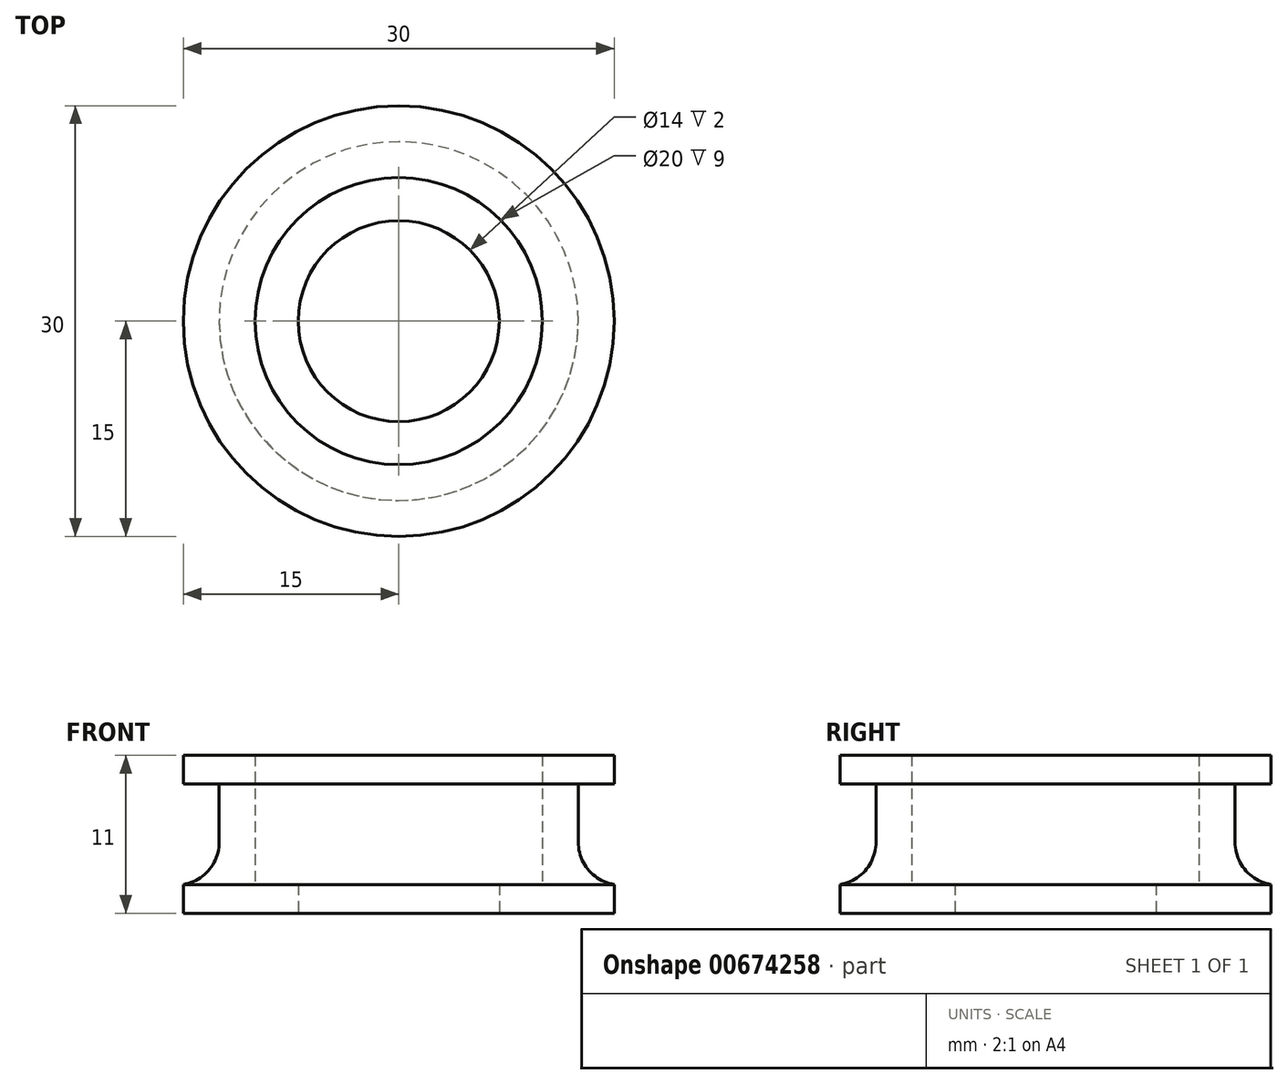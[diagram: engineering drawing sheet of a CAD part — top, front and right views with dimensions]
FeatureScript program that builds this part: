
annotation { "Feature Type Name" : "Feature", "Feature Type Description" : "" }
export const myFeature = defineFeature(function(context is Context, id is Id, definition is map)
    precondition{}
    {
        {
            var Q0;
            Q0=qCreatedBy(makeId("Top.planeOp"),FACE);
            var sketch = newSketch(context, id + "F0", { "sketchPlane" : qUnion([Q0])});
            skCircle(sketch, "E0", {"center": v(0, 0) * mm, "radius": 10 * mm});
            skCircle(sketch, "E1", {"center": v(0, 0) * mm, "radius": 15 * mm});
            skCircle(sketch, "E2", {"center": v(0, 0) * mm, "radius": 12.5 * mm});
            skCircle(sketch, "E3", {"center": v(0, 0) * mm, "radius": 7 * mm});
            skSolve(sketch);
        }
        {
            var Q0;
            Q0=makeQuery(id+"F0.imprint","IMPRINT",FACE,{"disambiguationData":[TD([[makeQuery(id+"F0.imprint","IMPRINT",EDGE,{"derivedFrom":sQuery(id+"F0.wireOp",EDGE,"E0")}),1.0]])]});
            var Q1;
            Q1=makeQuery(id+"F0.imprint","IMPRINT",FACE,{"disambiguationData":[TD([[makeQuery(id+"F0.imprint","IMPRINT",EDGE,{"derivedFrom":sQuery(id+"F0.wireOp",EDGE,"E0")}),-1.0]])]});
            var Q2;
            Q2=makeQuery(id+"F0.imprint","IMPRINT",FACE,{"disambiguationData":[TD([[makeQuery(id+"F0.imprint","IMPRINT",EDGE,{"derivedFrom":sQuery(id+"F0.wireOp",EDGE,"E1")}),1.0]])]});
            extrude(context, id + "F1", {"entities" : qUnion([Q0, Q1, Q2]), "depth" : 2 * mm, "offsetDistance" : 25 * mm});
        }
        {
            var Q0;
            Q0=makeQuery(id+"F0.imprint","IMPRINT",FACE,{"disambiguationData":[TD([[makeQuery(id+"F0.imprint","IMPRINT",EDGE,{"derivedFrom":sQuery(id+"F0.wireOp",EDGE,"E0")}),-1.0]])]});
            extrude(context, id + "F2", {"entities" : qUnion([Q0]), "operationType" : NewBodyOperationType.ADD, "depth" : 9 * mm, "offsetDistance" : 25 * mm});
        }
        {
            var Q0;
            Q0=makeQuery(id+"F2.opExtrude","CAP_FACE",FACE,{"disambiguationData":[OSD([sQuery(id+"F0.wireOp",EDGE,"E0"),sQuery(id+"F0.wireOp",EDGE,"E2")])],"isStart":false});
            var sketch = newSketch(context, id + "F3", { "sketchPlane" : qUnion([Q0])});
            skCircle(sketch, "E4", {"center": v(0, 0) * mm, "radius": 15 * mm});
            skCircle(sketch, "E5", {"center": v(0, 0) * mm, "radius": 10 * mm});
            skSolve(sketch);
        }
        {
            var Q0;
            Q0=makeQuery(id+"F3.imprint","IMPRINT",FACE,{"disambiguationData":[TD([[makeQuery(id+"F3.imprint","IMPRINT",EDGE,{"derivedFrom":sQuery(id+"F3.wireOp",EDGE,"E5")}),-1.0]])]});
            var Q1;
            Q1=makeQuery(id+"F3.imprint","IMPRINT",FACE,{"disambiguationData":[TD([[makeQuery(id+"F3.imprint","IMPRINT",EDGE,{"derivedFrom":sQuery(id+"F3.wireOp",EDGE,"E4")}),1.0]])]});
            extrude(context, id + "F4", {"entities" : qUnion([Q0, Q1]), "operationType" : NewBodyOperationType.ADD, "depth" : 2 * mm, "offsetDistance" : 25 * mm});
        }
        {
            var Q0;
            Q0=makeQuery(id+"F2.boolean.opBoolean","INTERSECT",EDGE,{"derivedFrom":[makeQuery(id+"F1.opExtrude","CAP_FACE",FACE,{"disambiguationData":[OSD([sQuery(id+"F0.wireOp",EDGE,"E1"),sQuery(id+"F0.wireOp",EDGE,"E3")])],"isStart":false}),makeQuery(id+"F2.opExtrude","SWEPT_FACE",FACE,{"disambiguationData":[OSD([sQuery(id+"F0.wireOp",EDGE,"E2")])]})]});
            var Q1;
            Q1=makeQuery(id+"F2.opExtrude","CAP_EDGE",EDGE,{"disambiguationData":[OSD([sQuery(id+"F0.wireOp",EDGE,"E2")])],"isStart":false});
            fillet(context, id + "F5", {"entities" : qUnion([Q0, Q1]), "radius" : 3 * mm, "tangentPropagation" : true, "allowEdgeOverflow" : false});
        }
    });
